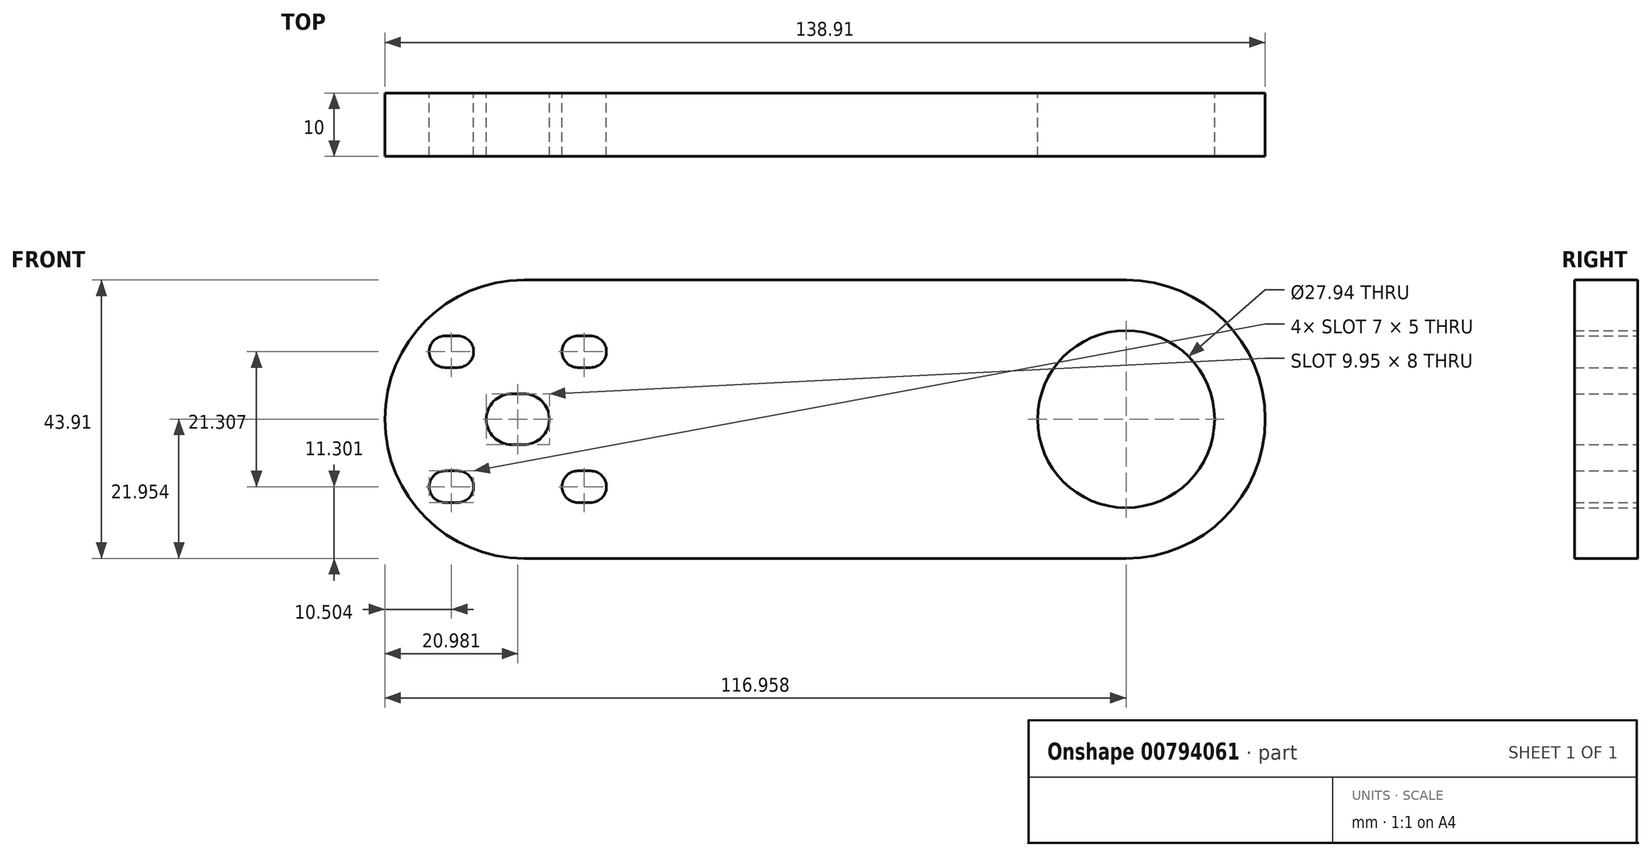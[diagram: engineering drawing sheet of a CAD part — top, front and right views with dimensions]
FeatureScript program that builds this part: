
annotation { "Feature Type Name" : "Feature", "Feature Type Description" : "" }
export const myFeature = defineFeature(function(context is Context, id is Id, definition is map)
    precondition{}
    {
        {
            var Q0;
            Q0=qCreatedBy(makeId("Front.planeOp"),FACE);
            var sketch = newSketch(context, id + "F0", { "sketchPlane" : qUnion([Q0])});
            skCircle(sketch, "E0", {"center": v(29.66, -109.85) * mm, "radius": 13.97 * mm});
            skArc(sketch, "E1", {"start": v(29.66, -131.8) * mm, "mid": v(51.61, -109.85) * mm, "end": v(29.66, -87.9) * mm});
            skArc(sketch, "E2", {"start": v(-65.34, -87.9) * mm, "mid": v(-87.3, -109.85) * mm, "end": v(-65.34, -131.8) * mm});
            skLineSegment(sketch, "E3", {"start": v(-65.34, -87.9) * mm, "end": v(29.66, -87.9) * mm});
            skLineSegment(sketch, "E4", {"start": v(-65.34, -131.8) * mm, "end": v(29.66, -131.8) * mm});
            skLineSegment(sketch, "E5", {"start": v(-87.3, -109.85) * mm, "end": v(-67.3, -109.85) * mm, "construction": true});
            skArc(sketch, "E6", {"start": v(-67.3, -105.85) * mm, "mid": v(-71.3, -109.85) * mm, "end": v(-67.3, -113.85) * mm});
            skArc(sketch, "E7", {"start": v(-65.34, -113.85) * mm, "mid": v(-61.34, -109.85) * mm, "end": v(-65.34, -105.85) * mm});
            skLineSegment(sketch, "E8", {"start": v(-67.3, -105.85) * mm, "end": v(-65.34, -105.85) * mm});
            skPoint(sketch, "E9.end.orphan", {"position": v(-65.34, -113.85) * mm});
            skLineSegment(sketch, "E10", {"start": v(-67.3, -113.85) * mm, "end": v(-65.34, -113.85) * mm});
            skLineSegment(sketch, "E11", {"start": v(-50.86, -123) * mm, "end": v(-25.65, -123) * mm, "construction": true});
            skLineSegment(sketch, "E12", {"start": v(-56.84, -131.8) * mm, "end": v(-56.84, -87.9) * mm, "construction": true});
            skArc(sketch, "E13", {"start": v(-56.84, -118) * mm, "mid": v(-59.34, -120.5) * mm, "end": v(-56.84, -123) * mm});
            skArc(sketch, "E14", {"start": v(-54.84, -123) * mm, "mid": v(-52.34, -120.5) * mm, "end": v(-54.84, -118) * mm});
            skLineSegment(sketch, "E15", {"start": v(-54.84, -123) * mm, "end": v(-56.84, -123) * mm});
            skLineSegment(sketch, "E16", {"start": v(-54.84, -118) * mm, "end": v(-56.84, -118) * mm});
            skLineSegment(sketch, "E17", {"start": v(-66.32, -105.85) * mm, "end": v(-66.32, -125.01) * mm, "construction": true});
            skLineSegment(sketch, "E18.MirrorCS", {"start": v(-54.84, -101.7) * mm, "end": v(-56.84, -101.7) * mm});
            skArc(sketch, "E19.MirrorCS", {"start": v(-54.84, -96.7) * mm, "mid": v(-52.34, -99.2) * mm, "end": v(-54.84, -101.7) * mm});
            skLineSegment(sketch, "E20.MirrorCS", {"start": v(-54.84, -96.7) * mm, "end": v(-56.84, -96.7) * mm});
            skArc(sketch, "E21.MirrorCS", {"start": v(-56.84, -101.7) * mm, "mid": v(-59.34, -99.2) * mm, "end": v(-56.84, -96.7) * mm});
            skLineSegment(sketch, "E22.MirrorCS", {"start": v(-77.8, -101.7) * mm, "end": v(-75.8, -101.7) * mm});
            skLineSegment(sketch, "E23.MirrorCS", {"start": v(-77.8, -96.7) * mm, "end": v(-75.8, -96.7) * mm});
            skLineSegment(sketch, "E24.MirrorCS", {"start": v(-77.8, -123) * mm, "end": v(-75.8, -123) * mm});
            skLineSegment(sketch, "E25.MirrorCS", {"start": v(-77.8, -118) * mm, "end": v(-75.8, -118) * mm});
            skArc(sketch, "E26.MirrorCS", {"start": v(-75.8, -118) * mm, "mid": v(-73.3, -120.5) * mm, "end": v(-75.8, -123) * mm});
            skArc(sketch, "E27.MirrorCS", {"start": v(-77.8, -96.7) * mm, "mid": v(-80.3, -99.2) * mm, "end": v(-77.8, -101.7) * mm});
            skArc(sketch, "E28.MirrorCS", {"start": v(-75.8, -101.7) * mm, "mid": v(-73.3, -99.2) * mm, "end": v(-75.8, -96.7) * mm});
            skArc(sketch, "E29.MirrorCS", {"start": v(-77.8, -123) * mm, "mid": v(-80.3, -120.5) * mm, "end": v(-77.8, -118) * mm});
            skSolve(sketch);
        }
        {
            var Q0;
            Q0=qSketchRegion(id+"F0",true);
            extrude(context, id + "F1", {"entities" : qUnion([Q0]), "depth" : 10 * mm, "offsetDistance" : 25 * mm});
        }
    });
